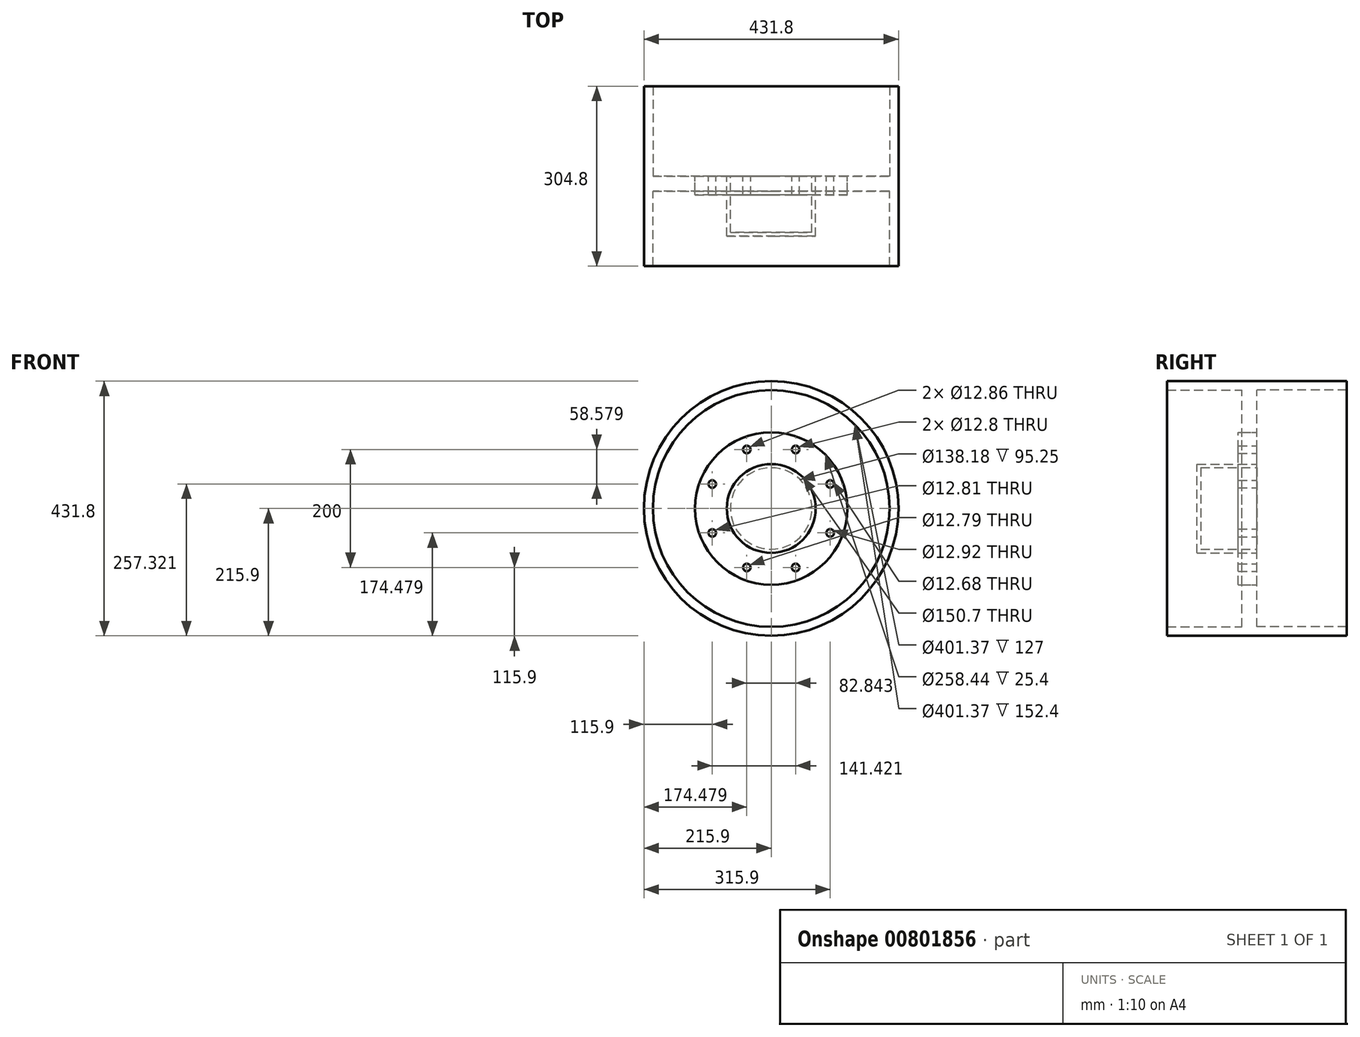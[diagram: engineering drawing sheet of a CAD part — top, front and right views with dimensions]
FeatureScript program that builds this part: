
annotation { "Feature Type Name" : "Feature", "Feature Type Description" : "" }
export const myFeature = defineFeature(function(context is Context, id is Id, definition is map)
    precondition{}
    {
        {
            var Q0;
            Q0=qCreatedBy(makeId("Front.planeOp"),FACE);
            var sketch = newSketch(context, id + "F0", { "sketchPlane" : qUnion([Q0])});
            skCircle(sketch, "E0", {"center": v(0, 0) * mm, "radius": 215.9 * mm});
            skCircle(sketch, "E1", {"center": v(0, 0) * mm, "radius": 200.69 * mm});
            skCircle(sketch, "E2", {"center": v(0, 0) * mm, "radius": 75.35 * mm});
            skCircle(sketch, "E3", {"center": v(-41.42, 100) * mm, "radius": 6.43 * mm});
            skCircle(sketch, "E4", {"center": v(41.42, 100) * mm, "radius": 6.4 * mm});
            skCircle(sketch, "E5", {"center": v(-100, 41.42) * mm, "radius": 6.4 * mm});
            skCircle(sketch, "E6", {"center": v(100, 41.42) * mm, "radius": 6.34 * mm});
            skCircle(sketch, "E7", {"center": v(100, -41.42) * mm, "radius": 6.46 * mm});
            skCircle(sketch, "E8", {"center": v(41.42, -100) * mm, "radius": 6.43 * mm});
            skCircle(sketch, "E9", {"center": v(-41.42, -100) * mm, "radius": 6.4 * mm});
            skCircle(sketch, "E10", {"center": v(-100, -41.42) * mm, "radius": 6.4 * mm});
            skCircle(sketch, "E11", {"center": v(0, 0) * mm, "radius": 129.22 * mm});
            skSolve(sketch);
        }
        {
            var Q0;
            Q0=makeQuery(id+"F0.imprint","IMPRINT",FACE,{"disambiguationData":[TD([[makeQuery(id+"F0.imprint","IMPRINT",EDGE,{"derivedFrom":sQuery(id+"F0.wireOp",EDGE,"E0")}),1.0]])]});
            extrude(context, id + "F1", {"entities" : qUnion([Q0]), "depth" : 152.4 * mm, "offsetDistance" : 25.4 * mm});
        }
        {
            var Q0;
            Q0=makeQuery(id+"F0.imprint","IMPRINT",FACE,{"disambiguationData":[TD([[makeQuery(id+"F0.imprint","IMPRINT",EDGE,{"derivedFrom":sQuery(id+"F0.wireOp",EDGE,"E1")}),1.0]])]});
            extrude(context, id + "F2", {"entities" : qUnion([Q0]), "operationType" : NewBodyOperationType.ADD, "depth" : 25.4 * mm, "offsetDistance" : 25.4 * mm});
        }
        {
            var Q0;
            Q0=makeQuery(id+"F0.imprint","IMPRINT",FACE,{"disambiguationData":[TD([[makeQuery(id+"F0.imprint","IMPRINT",EDGE,{"derivedFrom":sQuery(id+"F0.wireOp",EDGE,"E2")}),1.0]])]});
            extrude(context, id + "F3", {"entities" : qUnion([Q0]), "depth" : 101.6 * mm, "offsetDistance" : 25.4 * mm});
        }
        {
            var Q0;
            Q0=makeQuery(id+"F0.imprint","IMPRINT",FACE,{"disambiguationData":[TD([[makeQuery(id+"F0.imprint","IMPRINT",EDGE,{"derivedFrom":sQuery(id+"F0.wireOp",EDGE,"E2")}),-1.0]])]});
            extrude(context, id + "F4", {"entities" : qUnion([Q0]), "depth" : 31.75 * mm, "offsetDistance" : 25.4 * mm});
        }
        {
            var Q0;
            Q0=makeQuery(id+"F4.opExtrude","CAP_FACE",FACE,{"disambiguationData":[OSD([sQuery(id+"F0.wireOp",EDGE,"E2"),sQuery(id+"F0.wireOp",EDGE,"E3"),sQuery(id+"F0.wireOp",EDGE,"E4"),sQuery(id+"F0.wireOp",EDGE,"E5"),sQuery(id+"F0.wireOp",EDGE,"E6"),sQuery(id+"F0.wireOp",EDGE,"E7"),sQuery(id+"F0.wireOp",EDGE,"E8"),sQuery(id+"F0.wireOp",EDGE,"E9"),sQuery(id+"F0.wireOp",EDGE,"E10"),sQuery(id+"F0.wireOp",EDGE,"E11")])],"isStart":true});
            var sketch = newSketch(context, id + "F5", { "sketchPlane" : qUnion([Q0])});
            skCircle(sketch, "E12", {"center": v(0, 0) * mm, "radius": 69.1 * mm});
            skSolve(sketch);
        }
        {
            var Q0;
            Q0 = qSketchRegion(id + "F5", true);
            extrude(context, id + "F6", {"entities" : qUnion([Q0]), "operationType" : NewBodyOperationType.REMOVE, "oppositeDirection" : true, "depth" : 95.25 * mm, "offsetDistance" : 25.4 * mm});
        }
        {
            var Q0;
            Q0=makeQuery(id+"F1.opExtrude","CAP_FACE",FACE,{"disambiguationData":[OSD([sQuery(id+"F0.wireOp",EDGE,"E0"),sQuery(id+"F0.wireOp",EDGE,"E1")])],"isStart":false});
            extrude(context, id + "F7", {"entities" : qUnion([Q0]), "operationType" : NewBodyOperationType.ADD, "oppositeDirection" : true, "depth" : 304.8 * mm, "offsetDistance" : 25.4 * mm});
        }
    });
